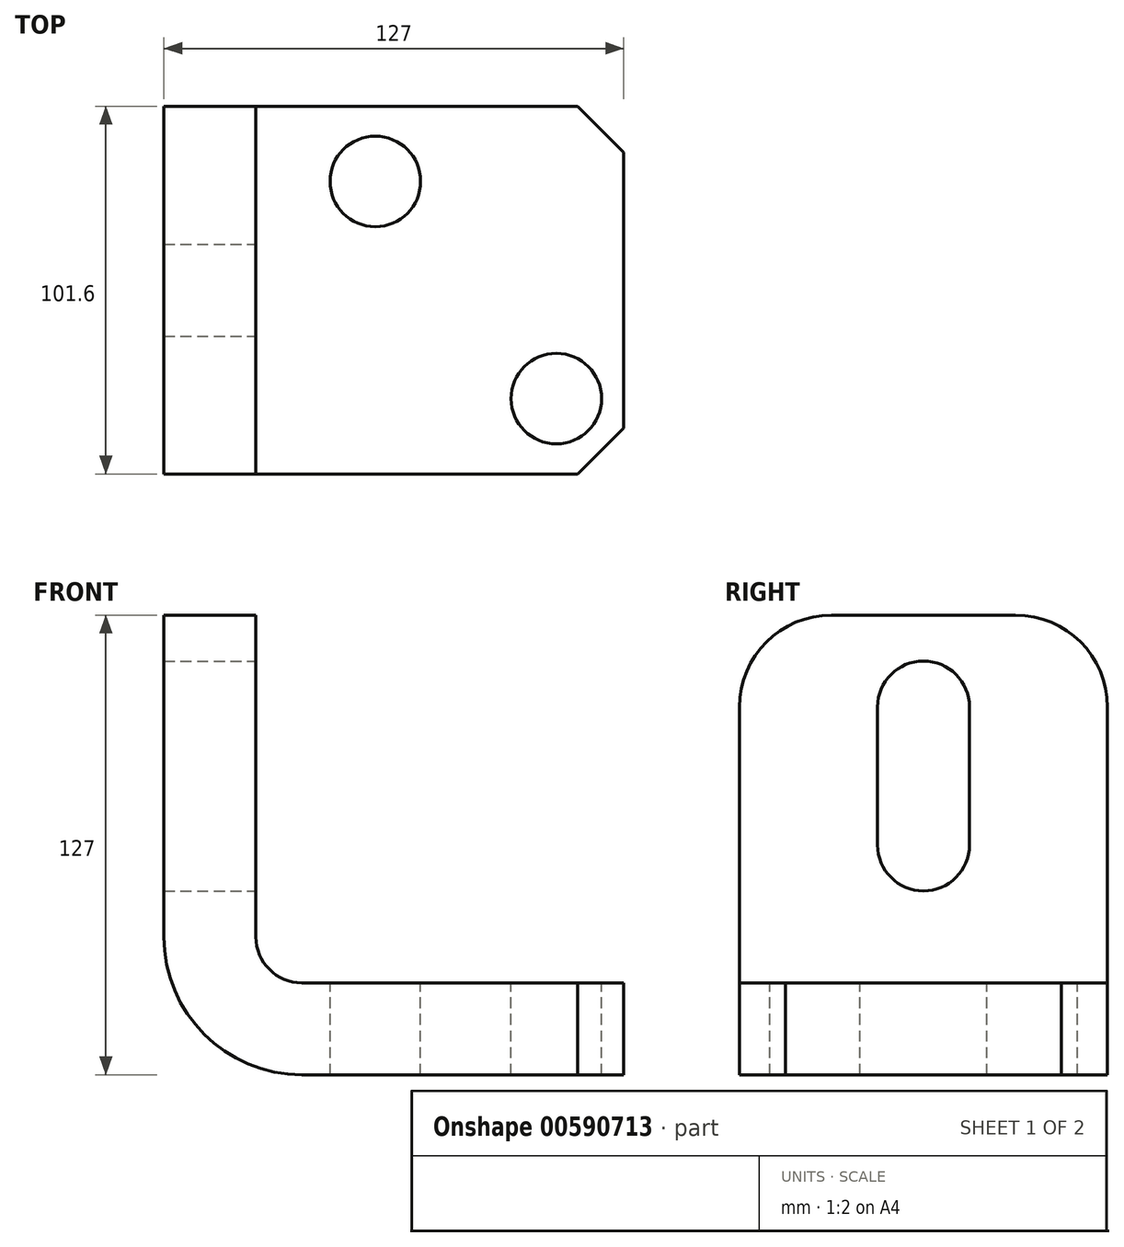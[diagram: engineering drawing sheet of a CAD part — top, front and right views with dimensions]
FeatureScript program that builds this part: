
annotation { "Feature Type Name" : "Feature", "Feature Type Description" : "" }
export const myFeature = defineFeature(function(context is Context, id is Id, definition is map)
    precondition{}
    {
        {
            var Q0;
            Q0=qCreatedBy(makeId("Front.planeOp"),FACE);
            var sketch = newSketch(context, id + "F0", { "sketchPlane" : qUnion([Q0])});
            skLineSegment(sketch, "E0", {"start": v(-58.4, 127) * mm, "end": v(-58.4, 38.1) * mm});
            skLineSegment(sketch, "E1", {"start": v(-20.3, 0) * mm, "end": v(68.6, 0) * mm});
            skLineSegment(sketch, "E2", {"start": v(68.6, 25.4) * mm, "end": v(68.6, 0) * mm});
            skLineSegment(sketch, "E3", {"start": v(68.6, 25.4) * mm, "end": v(-20.3, 25.4) * mm});
            skLineSegment(sketch, "E4", {"start": v(-33, 38.1) * mm, "end": v(-33, 127) * mm});
            skLineSegment(sketch, "E5", {"start": v(-33, 127) * mm, "end": v(-58.4, 127) * mm});
            skPoint(sketch, "E6.visualSharp", {"position": v(-58.4, 0) * mm});
            skArc(sketch, "E6.filletArc", {"start": v(-58.4, 38.1) * mm, "mid": v(-47.24, 11.16) * mm, "end": v(-20.3, 0) * mm});
            skPoint(sketch, "E7.visualSharp", {"position": v(-33, 25.4) * mm});
            skArc(sketch, "E7.filletArc", {"start": v(-33, 38.1) * mm, "mid": v(-29.27, 29.12) * mm, "end": v(-20.3, 25.4) * mm});
            skSolve(sketch);
        }
        {
            var Q0;
            Q0 = qSketchRegion(id + "F0", true);
            extrude(context, id + "F1", {"entities" : qUnion([Q0]), "oppositeDirection" : true, "depth" : 50.8 * mm, "offsetDistance" : 25.4 * mm, "hasSecondDirection" : true, "secondDirectionOppositeDirection" : false, "secondDirectionDepth" : 50.8 * mm});
        }
        {
            var Q0;
            Q0=makeQuery(id+"F1.opExtrude","SWEPT_FACE",FACE,{"disambiguationData":[OSD([sQuery(id+"F0.wireOp",EDGE,"E4")])]});
            var sketch = newSketch(context, id + "F2", { "sketchPlane" : qUnion([Q0])});
            skLineSegment(sketch, "E8", {"start": v(0, 101.6) * mm, "end": v(0, 63.5) * mm});
            skPoint(sketch, "E8.endSnap0", {"position": v(0, 127) * mm});
            skArc(sketch, "E9.0.startCap", {"start": v(-12.7, 101.6) * mm, "mid": v(0, 114.3) * mm, "end": v(12.7, 101.6) * mm});
            skArc(sketch, "E9.0.endCap", {"start": v(12.7, 63.5) * mm, "mid": v(0, 50.8) * mm, "end": v(-12.7, 63.5) * mm});
            skLineSegment(sketch, "E9.0.left", {"start": v(12.7, 101.6) * mm, "end": v(12.7, 63.5) * mm});
            skLineSegment(sketch, "E9.0.right", {"start": v(-12.7, 101.6) * mm, "end": v(-12.7, 63.5) * mm});
            skSolve(sketch);
        }
        {
            var Q0;
            Q0 = qSketchRegion(id + "F2", true);
            extrude(context, id + "F3", {"entities" : qUnion([Q0]), "operationType" : NewBodyOperationType.REMOVE, "oppositeDirection" : true, "depth" : 25.4 * mm, "offsetDistance" : 25.4 * mm});
        }
        {
            var Q0;
            Q0=makeQuery(id+"F1.opExtrude","SWEPT_FACE",FACE,{"disambiguationData":[OSD([sQuery(id+"F0.wireOp",EDGE,"E3")])]});
            var sketch = newSketch(context, id + "F4", { "sketchPlane" : qUnion([Q0])});
            skCircle(sketch, "E10", {"center": v(0, 30) * mm, "radius": 12.5 * mm});
            skCircle(sketch, "E11", {"center": v(50, -30) * mm, "radius": 12.5 * mm});
            skLineSegment(sketch, "E12", {"start": v(0, 30) * mm, "end": v(50, -30) * mm, "construction": true});
            skLineSegment(sketch, "E13", {"start": v(25, 0) * mm, "end": v(-20.3, 0) * mm, "construction": true});
            skLineSegment(sketch, "E14", {"start": v(-20.3, 0) * mm, "end": v(25, 0) * mm, "construction": true});
            skLineSegment(sketch, "E15", {"start": v(25, 0) * mm, "end": v(68.6, 0) * mm, "construction": true});
            skSolve(sketch);
        }
        {
            var Q0;
            Q0=makeQuery(id+"F4.imprint","IMPRINT",FACE,{"disambiguationData":[TD([[makeQuery(id+"F4.imprint","IMPRINT",EDGE,{"derivedFrom":sQuery(id+"F4.wireOp",EDGE,"E10")}),1.0]])]});
            var Q1;
            Q1=makeQuery(id+"F4.imprint","IMPRINT",FACE,{"disambiguationData":[TD([[makeQuery(id+"F4.imprint","IMPRINT",EDGE,{"derivedFrom":sQuery(id+"F4.wireOp",EDGE,"E11")}),1.0]])]});
            extrude(context, id + "F5", {"entities" : qUnion([Q0, Q1]), "operationType" : NewBodyOperationType.REMOVE, "oppositeDirection" : true, "depth" : 25.4 * mm, "offsetDistance" : 25.4 * mm});
        }
        {
            var Q0;
            Q0=makeQuery(id+"F1.opExtrude","CAP_EDGE",EDGE,{"disambiguationData":[OSD([sQuery(id+"F0.wireOp",EDGE,"E5")])],"isStart":true});
            var Q1;
            Q1=makeQuery(id+"F1.opExtrude","CAP_EDGE",EDGE,{"disambiguationData":[OSD([sQuery(id+"F0.wireOp",EDGE,"E5")])],"isStart":false});
            fillet(context, id + "F6", {"entities" : qUnion([Q0, Q1]), "radius" : 25.4 * mm, "tangentPropagation" : true, "allowEdgeOverflow" : false});
        }
        {
            var Q0;
            Q0=makeQuery(id+"F1.opExtrude","CAP_EDGE",EDGE,{"disambiguationData":[OSD([sQuery(id+"F0.wireOp",EDGE,"E2")])],"isStart":true});
            var Q1;
            Q1=makeQuery(id+"F1.opExtrude","CAP_EDGE",EDGE,{"disambiguationData":[OSD([sQuery(id+"F0.wireOp",EDGE,"E2")])],"isStart":false});
            chamfer(context, id + "F7", {"entities" : qUnion([Q0, Q1]), "width" : 12.7 * mm, "tangentPropagation" : true});
        }
    });
